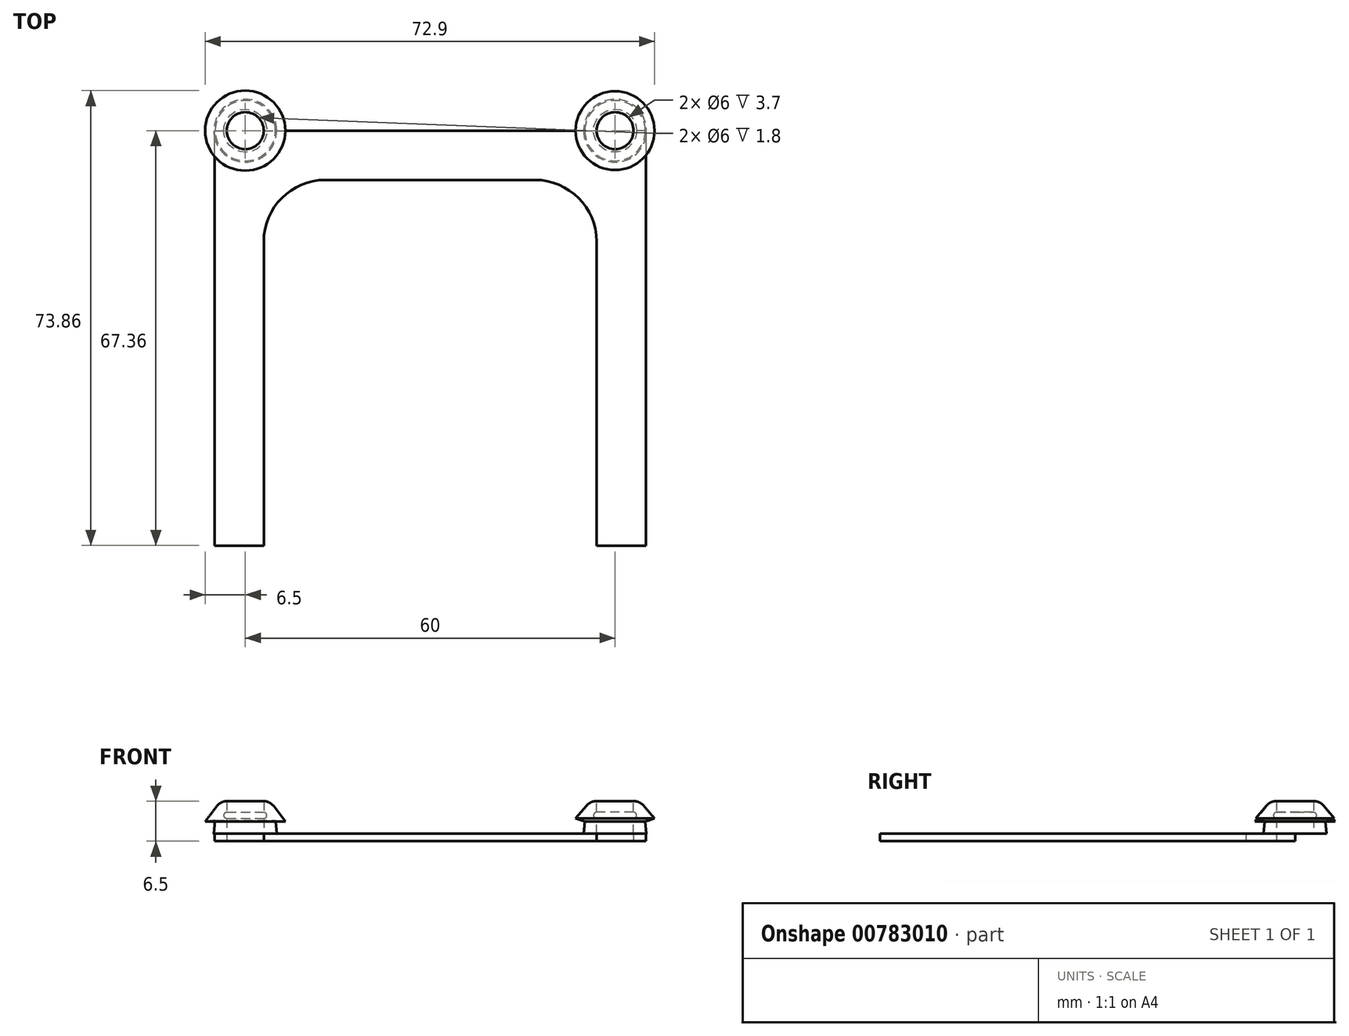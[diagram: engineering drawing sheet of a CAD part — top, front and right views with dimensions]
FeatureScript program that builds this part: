
annotation { "Feature Type Name" : "Feature", "Feature Type Description" : "" }
export const myFeature = defineFeature(function(context is Context, id is Id, definition is map)
    precondition{}
    {
        {
            var Q0;
            Q0=qCreatedBy(makeId("Front.planeOp"),FACE);
            var sketch = newSketch(context, id + "F0", { "sketchPlane" : qUnion([Q0])});
            skLineSegment(sketch, "E0", {"start": v(-3, 6.5) * mm, "end": v(-4, 6.5) * mm});
            skLineSegment(sketch, "E1", {"start": v(-4, 6.5) * mm, "end": v(-6.5, 3.2) * mm});
            skLineSegment(sketch, "E2", {"start": v(-6.5, 3.2) * mm, "end": v(-4.9, 3.4) * mm});
            skLineSegment(sketch, "E3", {"start": v(-3, 1.2) * mm, "end": v(-3, 3.7) * mm});
            skLineSegment(sketch, "E4", {"start": v(0, -15.71) * mm, "end": v(0, 21.33) * mm});
            skLineSegment(sketch, "E5", {"start": v(-5.1, 1.2) * mm, "end": v(-3, 1.2) * mm});
            skPoint(sketch, "E6.orphan", {"position": v(-3, 0) * mm});
            skLineSegment(sketch, "E7", {"start": v(-5.1, 1.2) * mm, "end": v(-4.9, 3.4) * mm});
            skArc(sketch, "E8", {"start": v(-3, 4.7) * mm, "mid": v(-3.5, 4.2) * mm, "end": v(-3, 3.7) * mm});
            skLineSegment(sketch, "E9.trimOffspring", {"start": v(-3, 4.7) * mm, "end": v(-3, 6.5) * mm});
            skSolve(sketch);
        }
        {
            var Q0;
            Q0=qSketchRegion(id+"F0",true);
            var Q1;
            Q1=sQuery(id+"F0.wireOp",EDGE,"E4");
            revolve(context, id + "F1", {"entities" : qUnion([Q0]), "axis" : qUnion([Q1]), "revolveType" : RevolveType.FULL});
        }
        {
            var Q0;
            Q0=qCreatedBy(makeId("Front.planeOp"),FACE);
            var sketch = newSketch(context, id + "F2", { "sketchPlane" : qUnion([Q0])});
            skLineSegment(sketch, "E10", {"start": v(60, 20.21) * mm, "end": v(60, -31.14) * mm});
            skLineSegment(sketch, "E11", {"start": v(57, 1.2) * mm, "end": v(54.9, 1.2) * mm});
            skLineSegment(sketch, "E12", {"start": v(54.9, 1.2) * mm, "end": v(55.1, 3.2) * mm});
            skLineSegment(sketch, "E13", {"start": v(53.6, 3.7) * mm, "end": v(56, 6.5) * mm});
            skLineSegment(sketch, "E14", {"start": v(56, 6.5) * mm, "end": v(57, 6.5) * mm});
            skLineSegment(sketch, "E15", {"start": v(57, 6.5) * mm, "end": v(57, 4.7) * mm});
            skLineSegment(sketch, "E16", {"start": v(53.6, 3.7) * mm, "end": v(55.1, 3.2) * mm});
            skArc(sketch, "E17", {"start": v(57, 4.7) * mm, "mid": v(56.5, 4.2) * mm, "end": v(57, 3.7) * mm});
            skLineSegment(sketch, "E18.trimOffspring", {"start": v(57, 3.7) * mm, "end": v(57, 1.2) * mm});
            skLineSegment(sketch, "E19", {"start": v(60, 1.2) * mm, "end": v(60, 0) * mm});
            skLineSegment(sketch, "E20", {"start": v(60, 0) * mm, "end": v(60, 1.2) * mm});
            skSolve(sketch);
        }
        {
            var Q0;
            Q0=makeQuery(id+"F2.imprint","IMPRINT",FACE,{"disambiguationData":[TD([[makeQuery(id+"F2.imprint","IMPRINT",EDGE,{"derivedFrom":sQuery(id+"F2.wireOp",EDGE,"E11")}),-1.0]])]});
            var Q1;
            Q1=sQuery(id+"F2.wireOp",EDGE,"E10");
            revolve(context, id + "F3", {"surfaceOperationType" : NewSurfaceOperationType.NEW, "entities" : qUnion([Q0]), "axis" : qUnion([Q1]), "revolveType" : RevolveType.FULL});
        }
        {
            var Q0;
            Q0=qCreatedBy(makeId("Top.planeOp"),FACE);
            var sketch = newSketch(context, id + "F4", { "sketchPlane" : qUnion([Q0])});
            skLineSegment(sketch, "E21.left", {"start": v(-5, -8) * mm, "end": v(-5, -67.36) * mm});
            skArc(sketch, "E22", {"start": v(0, -3) * mm, "mid": v(2.12, -2.12) * mm, "end": v(3, 0) * mm});
            skArc(sketch, "E23", {"start": v(57, 0) * mm, "mid": v(57.88, -2.12) * mm, "end": v(60, -3) * mm});
            skLineSegment(sketch, "E24.bottom", {"start": v(3, -8) * mm, "end": v(57, -8) * mm});
            skLineSegment(sketch, "E24.left", {"start": v(3, -8) * mm, "end": v(3, -67.36) * mm});
            skLineSegment(sketch, "E24.right", {"start": v(57, -8) * mm, "end": v(57, -67.36) * mm});
            skLineSegment(sketch, "E25.bottom", {"start": v(3, 0) * mm, "end": v(57, 0) * mm});
            skLineSegment(sketch, "E26.right", {"start": v(65, -8) * mm, "end": v(65, -67.36) * mm});
            skPoint(sketch, "E27.orphan", {"position": v(70, -145.73) * mm});
            skArc(sketch, "E28", {"start": v(57, 0) * mm, "mid": v(60, -3) * mm, "end": v(63, 0) * mm});
            skArc(sketch, "E29", {"start": v(-3, 0) * mm, "mid": v(0, -3) * mm, "end": v(3, 0) * mm});
            skPoint(sketch, "E30.trimOffspring.start.orphan", {"position": v(60, -145.73) * mm});
            skPoint(sketch, "E31.orphan", {"position": v(65, -145.73) * mm});
            skLineSegment(sketch, "E32.top", {"start": v(65, 0) * mm, "end": v(63, 0) * mm});
            skLineSegment(sketch, "E32.left", {"start": v(65, -8) * mm, "end": v(65, 0) * mm});
            skLineSegment(sketch, "E33.top", {"start": v(-5, 0) * mm, "end": v(-3, 0) * mm});
            skLineSegment(sketch, "E33.left", {"start": v(-5, -8) * mm, "end": v(-5, 0) * mm});
            skPoint(sketch, "E34.orphan", {"position": v(0, 3) * mm});
            skLineSegment(sketch, "E35", {"start": v(65, -67.36) * mm, "end": v(57, -67.36) * mm});
            skLineSegment(sketch, "E36.trimOffspring", {"start": v(3, -67.36) * mm, "end": v(-5, -67.36) * mm});
            skSolve(sketch);
        }
        {
            var Q0;
            Q0=qSketchRegion(id+"F4",true);
            extrude(context, id + "F5", {"entities" : qUnion([Q0]), "operationType" : NewBodyOperationType.ADD, "depth" : 1.2 * mm, "offsetDistance" : 25 * mm});
        }
        {
            var Q0;
            Q0=makeQuery(id+"F3.opRevolve","SWEPT_EDGE",EDGE,{"disambiguationData":[OSD([sQuery(id+"F2.wireOp",EDGE,"E13"),sQuery(id+"F2.wireOp",EDGE,"E14")])]});
            fillet(context, id + "F6", {"entities" : qUnion([Q0]), "radius" : 2 * mm, "tangentPropagation" : true, "allowEdgeOverflow" : false});
        }
        {
            var Q0;
            Q0=makeQuery(id+"F1.opRevolve","SWEPT_EDGE",EDGE,{"disambiguationData":[OSD([sQuery(id+"F0.wireOp",EDGE,"E0"),sQuery(id+"F0.wireOp",EDGE,"E1")])]});
            fillet(context, id + "F7", {"entities" : qUnion([Q0]), "radius" : 2 * mm, "tangentPropagation" : true, "allowEdgeOverflow" : false});
        }
        {
            var Q0;
            Q0=makeQuery(id+"F5.opExtrude","SWEPT_EDGE",EDGE,{"disambiguationData":[OSD([sQuery(id+"F4.wireOp",EDGE,"E24.bottom"),sQuery(id+"F4.wireOp",EDGE,"E24.left")])]});
            var Q1;
            Q1=makeQuery(id+"F5.opExtrude","SWEPT_EDGE",EDGE,{"disambiguationData":[OSD([sQuery(id+"F4.wireOp",EDGE,"E24.bottom"),sQuery(id+"F4.wireOp",EDGE,"E24.right")])]});
            fillet(context, id + "F8", {"entities" : qUnion([Q0, Q1]), "radius" : 10 * mm, "tangentPropagation" : true, "allowEdgeOverflow" : false});
        }
    });
